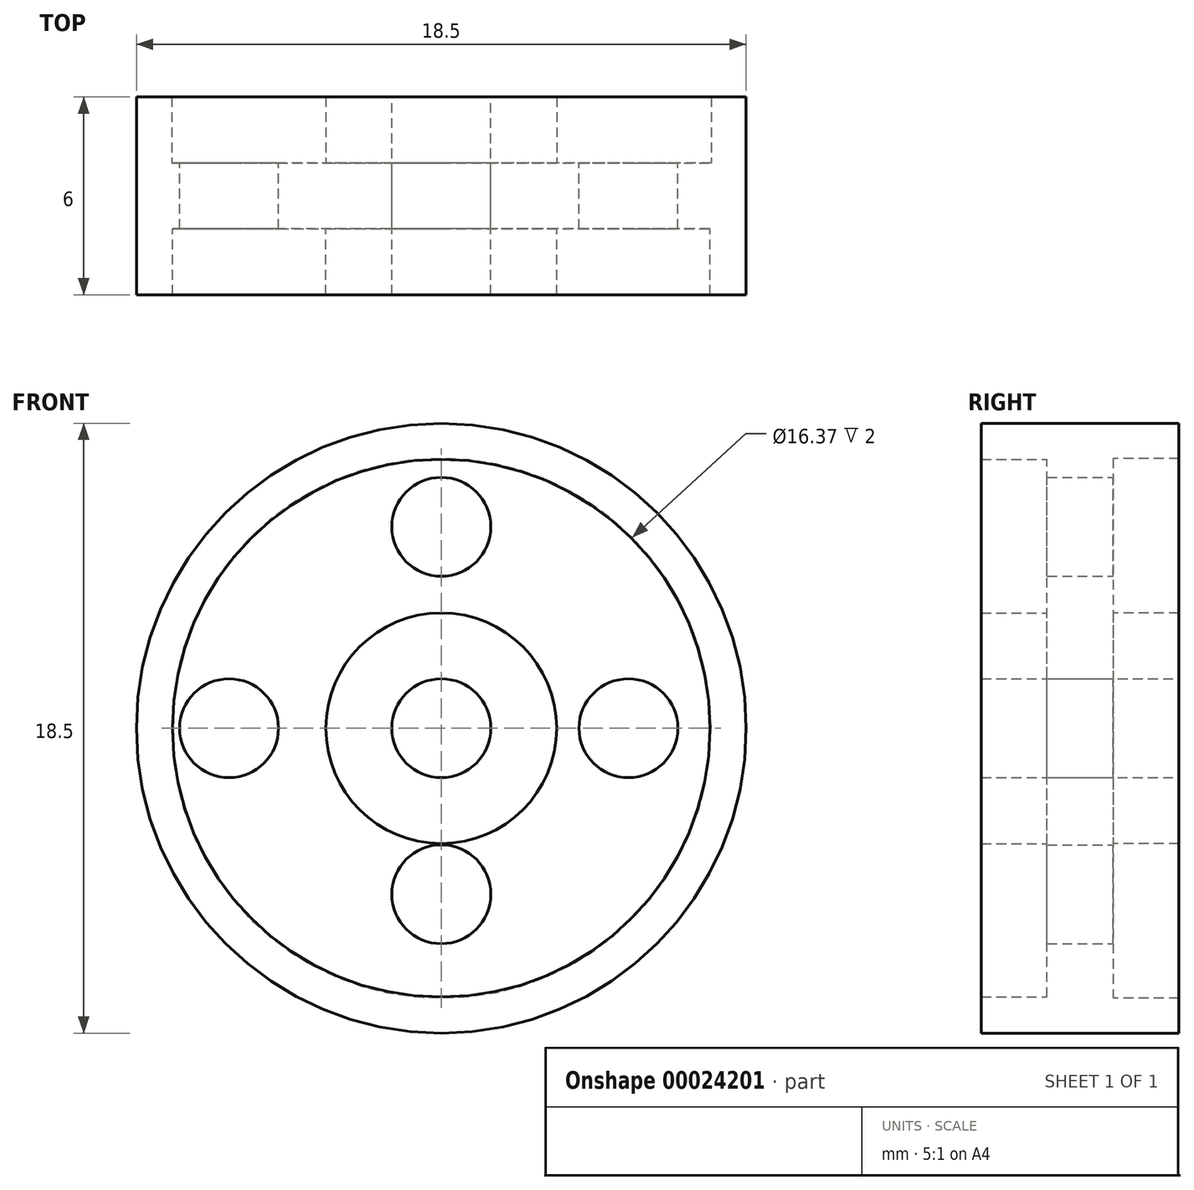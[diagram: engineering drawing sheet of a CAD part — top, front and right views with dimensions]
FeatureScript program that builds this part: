
annotation { "Feature Type Name" : "Feature", "Feature Type Description" : "" }
export const myFeature = defineFeature(function(context is Context, id is Id, definition is map)
    precondition{}
    {
        {
            var Q0;
            Q0=qCreatedBy(makeId("Front.planeOp"),FACE);
            var sketch = newSketch(context, id + "F0", { "sketchPlane" : qUnion([Q0])});
            skCircle(sketch, "E0", {"center": v(0, 0) * mm, "radius": 9.25 * mm});
            skCircle(sketch, "E1", {"center": v(0, -5.04) * mm, "radius": 1.5 * mm});
            skCircle(sketch, "E2", {"center": v(5.68, 0) * mm, "radius": 1.5 * mm});
            skCircle(sketch, "E3", {"center": v(0, 6.11) * mm, "radius": 1.5 * mm});
            skCircle(sketch, "E4", {"center": v(-6.44, 0) * mm, "radius": 1.5 * mm});
            skCircle(sketch, "E5", {"center": v(0, 0) * mm, "radius": 1.5 * mm});
            skSolve(sketch);
        }
        {
            var Q0;
            Q0 = qSketchRegion(id + "F0", true);
            extrude(context, id + "F1", {"entities" : qUnion([Q0]), "depth" : 2 * mm});
        }
        {
            var Q0;
            Q0=makeQuery(id+"F1.opExtrude","CAP_FACE",FACE,{"disambiguationData":[OSD([sQuery(id+"F0.wireOp",EDGE,"E0"),sQuery(id+"F0.wireOp",EDGE,"E1"),sQuery(id+"F0.wireOp",EDGE,"E2"),sQuery(id+"F0.wireOp",EDGE,"E3"),sQuery(id+"F0.wireOp",EDGE,"E4"),sQuery(id+"F0.wireOp",EDGE,"E5")])],"isStart":false});
            var sketch = newSketch(context, id + "F2", { "sketchPlane" : qUnion([Q0])});
            skCircle(sketch, "E6", {"center": v(0, 0) * mm, "radius": 3.5 * mm});
            skSolve(sketch);
        }
        {
            var Q0;
            Q0 = qSketchRegion(id + "F2", true);
            extrude(context, id + "F3", {"entities" : qUnion([Q0]), "operationType" : NewBodyOperationType.ADD, "depth" : 2 * mm});
        }
        {
            var Q0;
            Q0=makeQuery(id+"F3.opExtrude","CAP_FACE",FACE,{"disambiguationData":[OSD([sQuery(id+"F2.wireOp",EDGE,"E6")])],"isStart":false});
            var sketch = newSketch(context, id + "F4", { "sketchPlane" : qUnion([Q0])});
            skCircle(sketch, "E7", {"center": v(0, 0) * mm, "radius": 1.5 * mm});
            skSolve(sketch);
        }
        {
            var Q0;
            Q0=makeQuery(id+"F4.imprint","IMPRINT",FACE,{"disambiguationData":[TD([[makeQuery(id+"F4.imprint","IMPRINT",EDGE,{"derivedFrom":sQuery(id+"F4.wireOp",EDGE,"E7")}),1.0]])]});
            extrude(context, id + "F5", {"entities" : qUnion([Q0]), "operationType" : NewBodyOperationType.REMOVE, "oppositeDirection" : true, "depth" : 25.4 * mm});
        }
        {
            var Q0;
            Q0=makeQuery(id+"F1.opExtrude","CAP_FACE",FACE,{"disambiguationData":[OSD([sQuery(id+"F0.wireOp",EDGE,"E0"),sQuery(id+"F0.wireOp",EDGE,"E1"),sQuery(id+"F0.wireOp",EDGE,"E2"),sQuery(id+"F0.wireOp",EDGE,"E3"),sQuery(id+"F0.wireOp",EDGE,"E4"),sQuery(id+"F0.wireOp",EDGE,"E5")])],"isStart":true});
            var sketch = newSketch(context, id + "F6", { "sketchPlane" : qUnion([Q0])});
            skCircle(sketch, "E8", {"center": v(0, 0) * mm, "radius": 3.5 * mm});
            skSolve(sketch);
        }
        {
            var Q0;
            Q0 = qSketchRegion(id + "F6", true);
            extrude(context, id + "F7", {"entities" : qUnion([Q0]), "operationType" : NewBodyOperationType.ADD, "depth" : 2 * mm});
        }
        {
            var Q0;
            Q0=makeQuery(id+"F7.opExtrude","CAP_FACE",FACE,{"disambiguationData":[OSD([sQuery(id+"F6.wireOp",EDGE,"E8")])],"isStart":false});
            var sketch = newSketch(context, id + "F8", { "sketchPlane" : qUnion([Q0])});
            skCircle(sketch, "E9", {"center": v(0, 0) * mm, "radius": 1.5 * mm});
            skSolve(sketch);
        }
        {
            var Q0;
            Q0=makeQuery(id+"F8.imprint","IMPRINT",FACE,{"disambiguationData":[TD([[makeQuery(id+"F8.imprint","IMPRINT",EDGE,{"derivedFrom":sQuery(id+"F8.wireOp",EDGE,"E9")}),1.0]])]});
            extrude(context, id + "F9", {"entities" : qUnion([Q0]), "operationType" : NewBodyOperationType.REMOVE, "oppositeDirection" : true, "depth" : 25.4 * mm});
        }
        {
            var Q0;
            Q0=makeQuery(id+"F1.opExtrude","CAP_FACE",FACE,{"disambiguationData":[OSD([sQuery(id+"F0.wireOp",EDGE,"E0"),sQuery(id+"F0.wireOp",EDGE,"E1"),sQuery(id+"F0.wireOp",EDGE,"E2"),sQuery(id+"F0.wireOp",EDGE,"E3"),sQuery(id+"F0.wireOp",EDGE,"E4"),sQuery(id+"F0.wireOp",EDGE,"E5")])],"isStart":false});
            var sketch = newSketch(context, id + "F10", { "sketchPlane" : qUnion([Q0])});
            skCircle(sketch, "E10", {"center": v(0, 0) * mm, "radius": 8.16 * mm});
            skSolve(sketch);
        }
        {
            var Q0;
            Q0=makeQuery(id+"F10.imprint","IMPRINT",FACE,{"disambiguationData":[TD([[makeQuery(id+"F10.imprint","IMPRINT",EDGE,{"derivedFrom":sQuery(id+"F10.wireOp",EDGE,"E10")}),-1.0]])]});
            extrude(context, id + "F11", {"entities" : qUnion([Q0]), "operationType" : NewBodyOperationType.ADD, "depth" : 2 * mm});
        }
        {
            var Q0;
            Q0=makeQuery(id+"F1.opExtrude","CAP_FACE",FACE,{"disambiguationData":[OSD([sQuery(id+"F0.wireOp",EDGE,"E0"),sQuery(id+"F0.wireOp",EDGE,"E1"),sQuery(id+"F0.wireOp",EDGE,"E2"),sQuery(id+"F0.wireOp",EDGE,"E3"),sQuery(id+"F0.wireOp",EDGE,"E4"),sQuery(id+"F0.wireOp",EDGE,"E5")])],"isStart":true});
            var sketch = newSketch(context, id + "F12", { "sketchPlane" : qUnion([Q0])});
            skCircle(sketch, "E11", {"center": v(0, 0) * mm, "radius": 8.19 * mm});
            skSolve(sketch);
        }
        {
            var Q0;
            Q0=makeQuery(id+"F12.imprint","IMPRINT",FACE,{"disambiguationData":[TD([[makeQuery(id+"F12.imprint","IMPRINT",EDGE,{"derivedFrom":sQuery(id+"F12.wireOp",EDGE,"E11")}),-1.0]])]});
            extrude(context, id + "F13", {"entities" : qUnion([Q0]), "operationType" : NewBodyOperationType.ADD, "depth" : 2 * mm});
        }
    });
